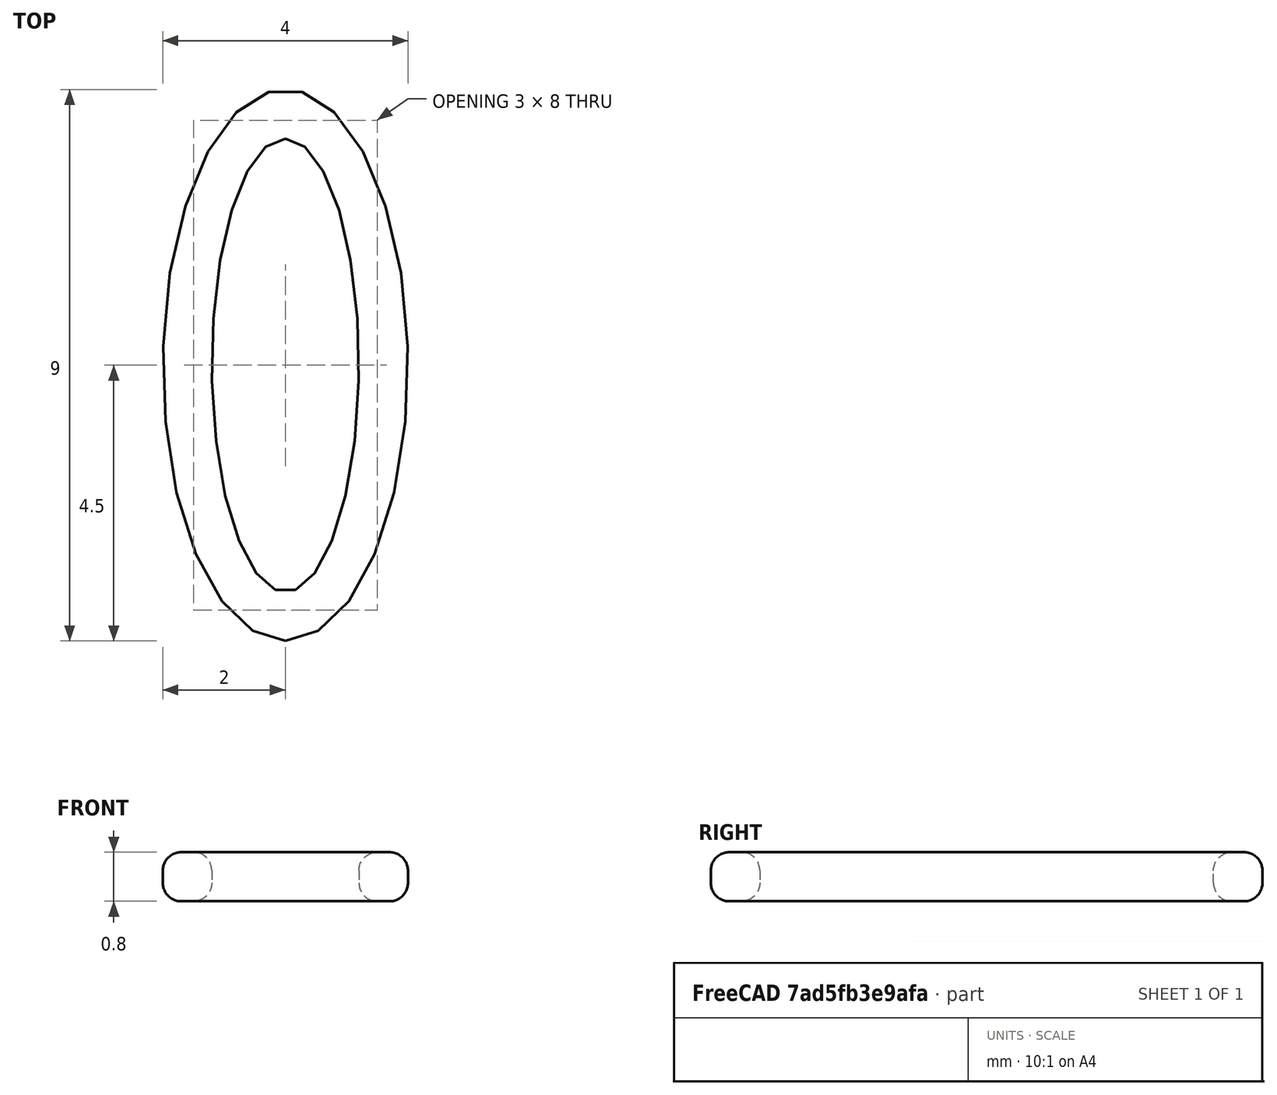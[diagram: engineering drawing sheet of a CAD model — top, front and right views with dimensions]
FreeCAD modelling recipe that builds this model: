
FCSTD DOCUMENT  (FreeCAD 0.16R6712 (Git))
Label: 0f
License: All rights reserved
LicenseURL: http://en.wikipedia.org/wiki/All_rights_reserved
objects: Sketcher::SketchObject×1, PartDesign::Pad×1, PartDesign::Fillet×1, Mesh::Feature×1
note: 4 computed .brp shape members not serialized (recipe doc carries the construction recipe); baked Part::Feature solids carry a one-line shape summary decoded from their .brp

FEATURE [Sketcher::SketchObject] Sketch
  sketch-geometry (10):
    g0: Ellipse CenterX=0 CenterY=4.5 CenterZ=0 NormalX=0 NormalY=0 NormalZ=1 MajorRadius=4.5 MinorRadius=2 AngleXU=-1.5708
    g1: LineSegment [constr] StartX=0 StartY=0 StartZ=0 EndX=0 EndY=9 EndZ=0
    g2: LineSegment [constr] StartX=2 StartY=4.5 StartZ=0 EndX=-2 EndY=4.5 EndZ=0
    g3: GeomPoint [constr] X=0 Y=0.468871 Z=0
    g4: GeomPoint [constr] X=0 Y=8.53113 Z=0
    g5: Ellipse CenterX=0 CenterY=4.5 CenterZ=0 NormalX=0 NormalY=0 NormalZ=1 MajorRadius=3.7 MinorRadius=1.2 AngleXU=1.5708
    g6: LineSegment [constr] StartX=0 StartY=8.2 StartZ=0 EndX=0 EndY=0.8 EndZ=0
    g7: LineSegment [constr] StartX=-1.2 StartY=4.5 StartZ=0 EndX=1.2 EndY=4.5 EndZ=0
    g8: GeomPoint [constr] X=0 Y=8 Z=0
    g9: GeomPoint [constr] X=0 Y=1 Z=0
  constraints (11):
    c: InternalAlignment(g1-g4 -> g0) x4
    c: PointOnObject(g0,g-2)
    c: PointOnObject(g-1,g0)
    c: Distance(g2,g0) = 2
    c: PointOnObject(g1,g-2)
    c: InternalAlignment(g6-g9 -> g5) x4
    c: Coincident(g5,g0)
    c: DistanceY(g-1,g0) = 4.5
    c: DistanceY(g6,g1) = 0.8
    c: DistanceX(g7,g2) = 0.8
    c: PointOnObject(g6,g-2)
FEATURE [PartDesign::Pad] Pad
  Length = 0.8
  Length2 = 100
  Midplane = true
  Sketch = -> Sketch
  Type = 0
FEATURE [PartDesign::Fillet] Fillet
  Base = -> Pad [Edge3,Edge6,Edge2,Edge5]
  Radius = 0.3
FEATURE [Mesh::Feature] Mesh  label="Fillet (Meshed)"
